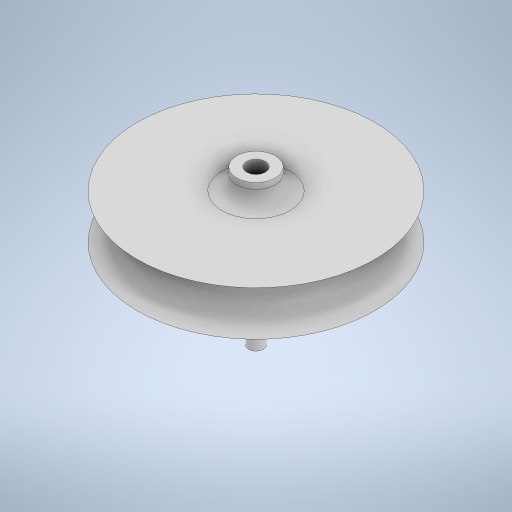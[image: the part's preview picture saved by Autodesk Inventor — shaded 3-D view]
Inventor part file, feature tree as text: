
AUTODESK INVENTOR PART (.ipt)
format: ipt  version: 2024 (Build 280153000, 153)  size: 302,080 bytes
history: native  units: in
note: dims shown in document units (in); Inventor stores cm internally (conversion verified against a paired STEP export)
features: sketch x7, extrude x5, fillet x3, sweep x1
ambient origin geometry x8: Origin, YZ Plane, XZ Plane, XY Plane, X Axis, Y Axis, Z Axis, Center Point
bodies: Solid1 (feature_tree)
feature tree (16):
  extrude  "Extrusion1"  Depth=0.5906in TaperAngle=0.0deg
  sweep  "Sweep1"
  extrude  "Extrusion2"  Depth=0.2756in TaperAngle=0.0deg
  extrude  "Extrusion3"  Depth=0.1181in TaperAngle=0.0deg
  extrude  "Extrusion4"  Depth=0.5906in TaperAngle=0.0deg
  extrude  "Extrusion5"  Depth=0.1969in TaperAngle=0.0deg
  fillet  "Fillet1"  Radius=0.1969in
  fillet  "Fillet2"  Radius=0.1969in
  fillet  "Fillet3"  Radius=0.1969in
  sketch  "Sketch1"  dims[d0=3.1496in d1=0.5906in d2=0.0in]
  sketch  "Sketch2"  dims[d3=0.0in d4=0.0in d5=0.248in]
  sketch  "3D Sketch1"
  sketch  "Sketch3"  dims[d6=0.5118in d7=0.2756in d8=0.0in]
  sketch  "Sketch4"  dims[d9=0.5118in d10=0.1181in d11=0.0in]
  sketch  "Sketch5"  dims[d12=0.248in d13=0.5906in d14=0.0in]
  sketch  "Sketch6"  dims[d15=0.1969in d16=1.063in d17=0.0in d18=0.1969in d19=0.1969in d20=0.1969in]
